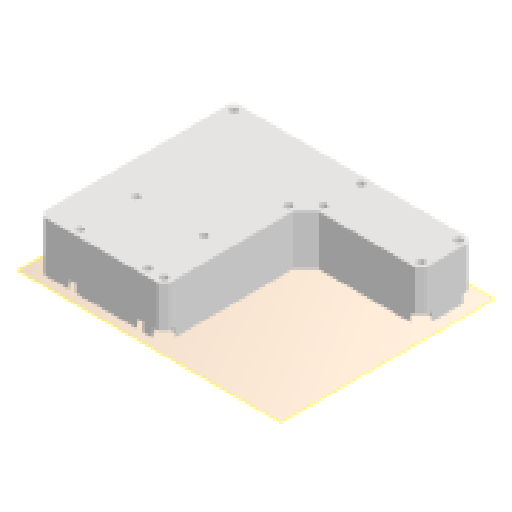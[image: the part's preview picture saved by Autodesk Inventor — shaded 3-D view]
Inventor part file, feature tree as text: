
AUTODESK INVENTOR PART (.ipt)
format: ipt  version: 2024.1 (Build 281209000, 209)  size: 149,504 bytes
history: native  units: mm
features: other x3, plane x2, sketch x2, reference x2, extrude x1, chamfer x1, hole x1
ambient origin geometry x8: Origin, YZ Plane, XZ Plane, XY Plane, X Axis, Y Axis, Z Axis, Center Point
bodies: Volumenkörper1 (feature_tree)
feature tree (12):
  plane  "Arbeitsebene1"
  plane  "Arbeitsebene2"
  extrude  "Extrusion1"  Depth=10.0mm TaperAngle=45.0deg
  chamfer  "Fasen1"  [1 undecoded]
  hole  "Bohrung1"  [1 undecoded]
  sketch  "Skizze1"  dims[d0=10.0mm d1=0.0mm d2=2.0mm d3=2.0mm d4=45.0deg]
  reference  "Referenz1"
  sketch  "Skizze2"  dims[d5=2.8mm d6=6.0mm d7=6.5mm d8=3.5mm d9=90.0deg d10=20.0mm d11=0.0mm]
  reference  "Referenz2"
  other  "Assembly_MicroscopeInABox_v0.iam"
  other  "MIAB_Case_v0_MIR:1"
  other  "MIAB_Case_v0:1"
note: 2 required parameter values undecoded (feature->parameter linkage not recoverable at this tier; creation-order binding heuristic only, values carry confidence <= 0.55)
